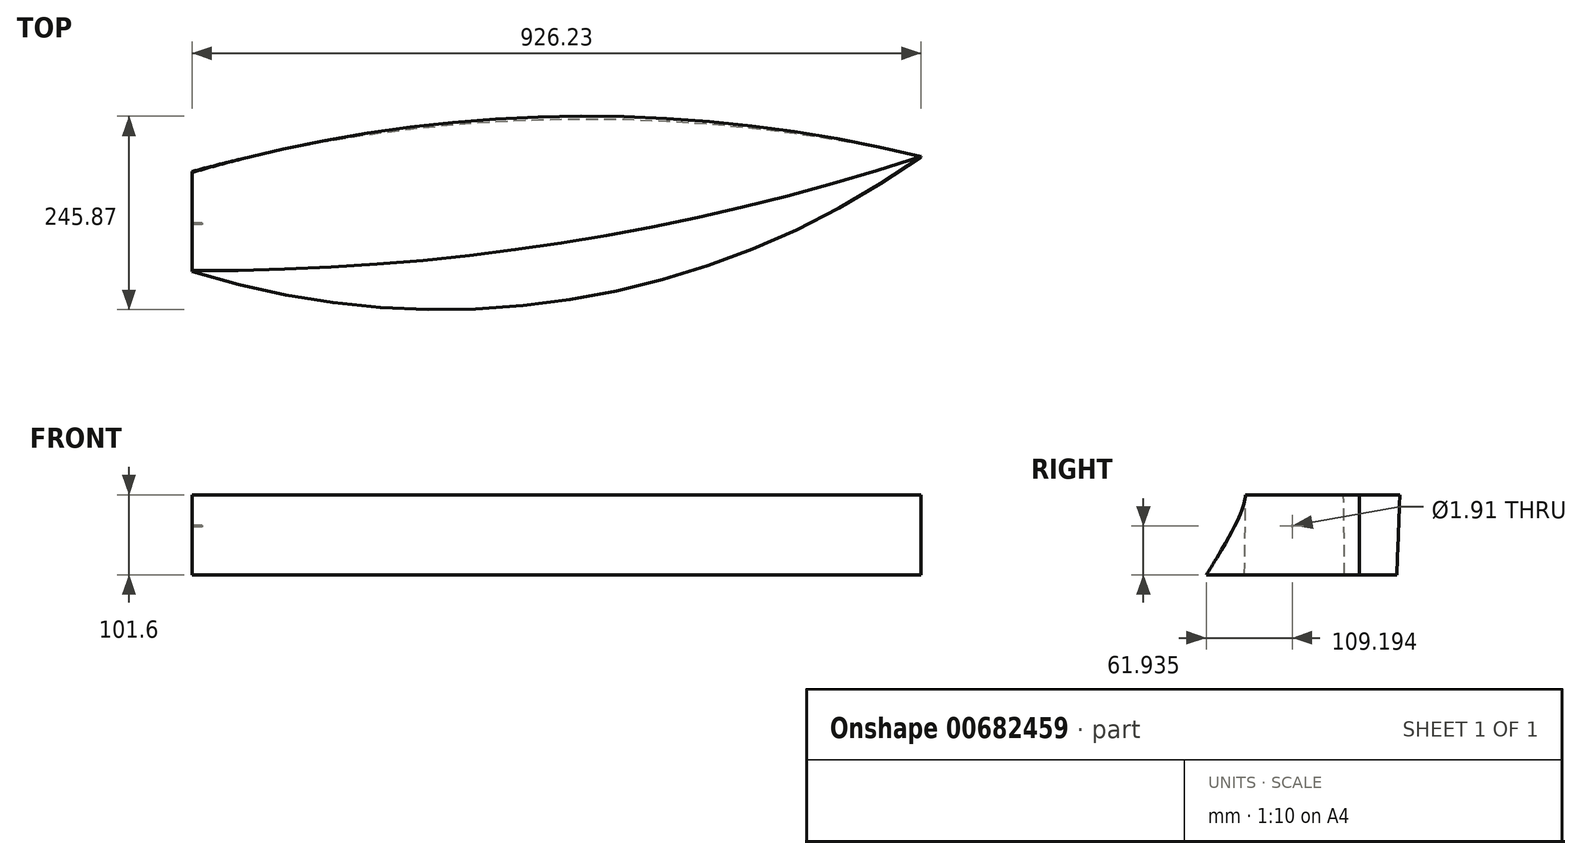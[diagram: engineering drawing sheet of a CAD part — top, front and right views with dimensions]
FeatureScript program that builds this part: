
annotation { "Feature Type Name" : "Feature", "Feature Type Description" : "" }
export const myFeature = defineFeature(function(context is Context, id is Id, definition is map)
    precondition{}
    {
        {
            var Q0;
            Q0=qCreatedBy(makeId("Top.planeOp"),FACE);
            var sketch = newSketch(context, id + "F0", { "sketchPlane" : qUnion([Q0])});
            skArc(sketch, "E0", {"start": v(926.2, 82.05) * mm, "mid": v(461.97, 129.42) * mm, "end": v(0, 63.5) * mm});
            skArc(sketch, "E1", {"start": v(0, -63.5) * mm, "mid": v(480.17, -99.36) * mm, "end": v(926.2, 82.05) * mm});
            skLineSegment(sketch, "E2", {"start": v(0, -63.5) * mm, "end": v(0, 63.5) * mm});
            skPoint(sketch, "E3.center.orphan", {"position": v(0, 0) * mm});
            skSolve(sketch);
        }
        {
            var Q0;
            Q0=qCreatedBy(makeId("Top.planeOp"),FACE);
            cPlane(context, id + "F1", {"entities" : qUnion([Q0]), "cplaneType" : CPlaneType.OFFSET, "offset" : 101.6 * mm, "width" : 152.4 * mm, "height" : 152.4 * mm});
        }
        {
            var Q0;
            Q0=qCreatedBy(id+"F1.planeOp",FACE);
            var sketch = newSketch(context, id + "F2", { "sketchPlane" : qUnion([Q0])});
            skArc(sketch, "E4", {"start": v(926.23, 82.5) * mm, "mid": v(461.78, 133.3) * mm, "end": v(0, 62.24) * mm});
            skArc(sketch, "E5", {"start": v(0, -62.24) * mm, "mid": v(468.99, -27.44) * mm, "end": v(926.23, 82.5) * mm});
            skLineSegment(sketch, "E6", {"start": v(0, 62.24) * mm, "end": v(0, -62.24) * mm});
            skSolve(sketch);
        }
        {
            var Q0;
            Q0=makeQuery(id+"F0.imprint","IMPRINT",FACE,{"disambiguationData":[TD([[makeQuery(id+"F0.imprint","IMPRINT",EDGE,{"derivedFrom":sQuery(id+"F0.wireOp",EDGE,"E0")}),1.0]])]});
            var Q1;
            Q1=makeQuery(id+"F2.imprint","IMPRINT",FACE,{"disambiguationData":[TD([[makeQuery(id+"F2.imprint","IMPRINT",EDGE,{"derivedFrom":sQuery(id+"F2.wireOp",EDGE,"E4")}),1.0]])]});
            loft(context, id + "F3", {"sheetProfilesArray" : [{ "sheetProfileEntities" : qUnion([Q0]) }, { "sheetProfileEntities" : qUnion([Q1]) }]});
        }
        {
            var Q0;
            Q0=qCreatedBy(makeId("Right.planeOp"),FACE);
            var sketch = newSketch(context, id + "F4", { "sketchPlane" : qUnion([Q0])});
            skPoint(sketch, "E7", {"position": v(-2.95, 61.94) * mm});
            skSolve(sketch);
        }
        {
            var Q0;
            Q0=sQuery(id+"F4.wireOp",VERTEX,"E7");
            var Q1;
            Q1=makeQuery(id+"F3.opLoft","SWEPT_BODY",BODY,{"disambiguationData":[OSD([makeQuery(id+"F0.imprint","IMPRINT",FACE,{"disambiguationData":[TD([[makeQuery(id+"F0.imprint","IMPRINT",EDGE,{"derivedFrom":sQuery(id+"F0.wireOp",EDGE,"E0")}),1.0]])]}),makeQuery(id+"F2.imprint","IMPRINT",FACE,{"disambiguationData":[TD([[makeQuery(id+"F2.imprint","IMPRINT",EDGE,{"derivedFrom":sQuery(id+"F2.wireOp",EDGE,"E4")}),1.0]])]})])]});
            hole(context, id + "F5", {"style" : HoleStyle.SIMPLE, "endStyle" : HoleEndStyle.BLIND, "oppositeDirection" : true, "holeDiameter" : 1.9 * mm, "majorDiameter" : 6.35 * mm, "holeDepth" : 12.7 * mm, "isTappedThrough" : true, "tappedDepth" : 12.7 * mm, "tapClearance" : 3, "locations" : qUnion([Q0]), "scope" : qUnion([Q1])});
        }
    });
